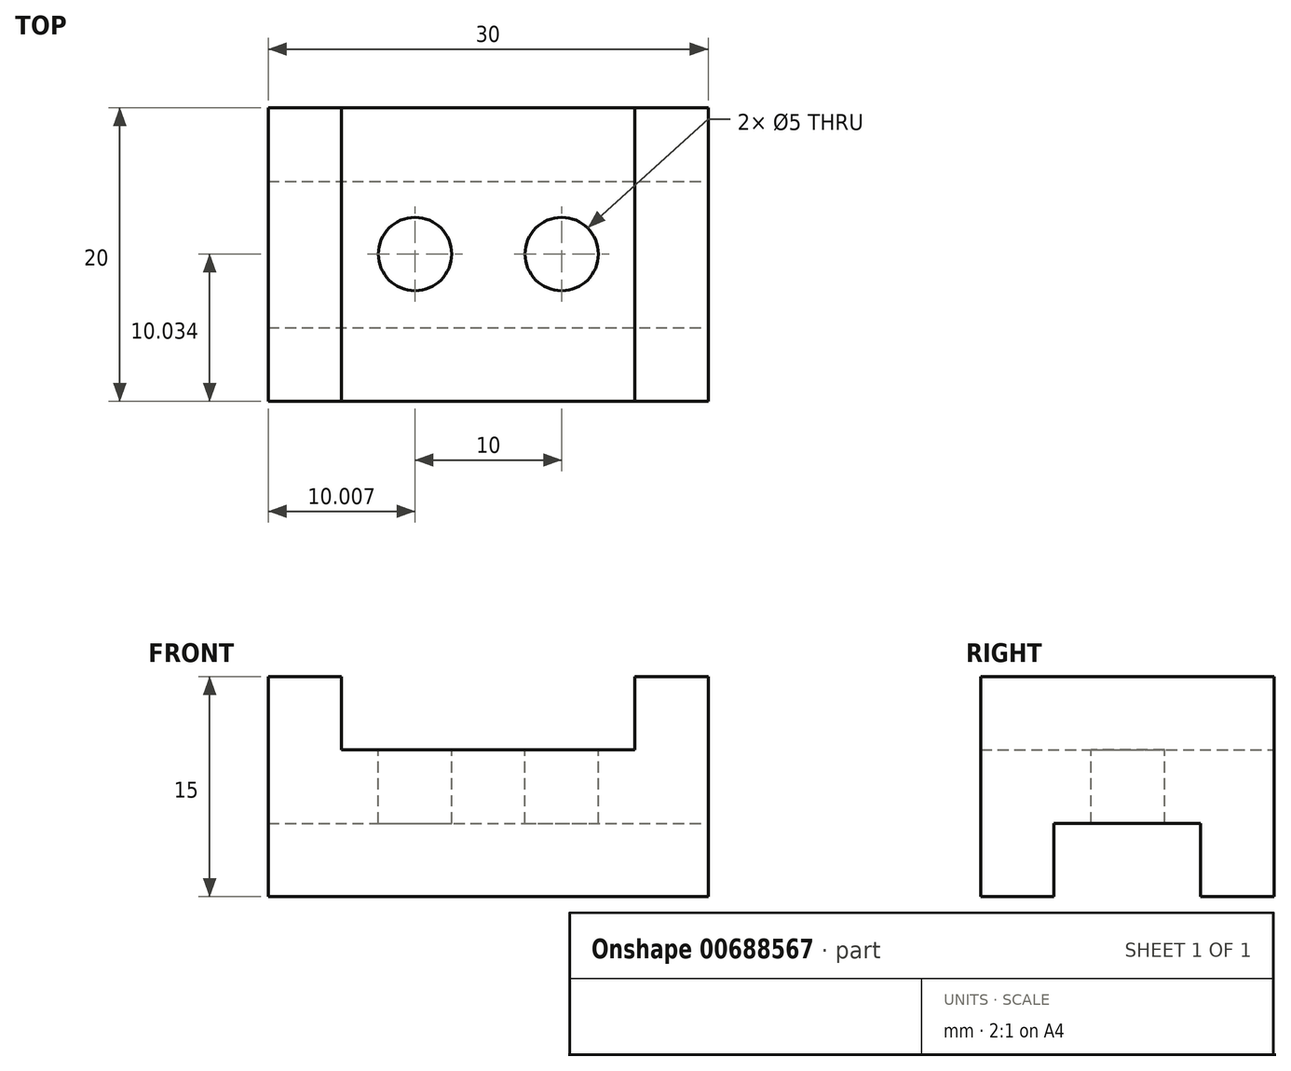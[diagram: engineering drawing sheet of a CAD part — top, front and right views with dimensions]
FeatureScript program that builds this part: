
annotation { "Feature Type Name" : "Feature", "Feature Type Description" : "" }
export const myFeature = defineFeature(function(context is Context, id is Id, definition is map)
    precondition{}
    {
        {
            var Q0;
            Q0=qCreatedBy(makeId("Top.planeOp"),FACE);
            var sketch = newSketch(context, id + "F0", { "sketchPlane" : qUnion([Q0])});
            skLineSegment(sketch, "E0.bottom", {"start": v(19.3, -0.64) * mm, "end": v(-10.7, -0.64) * mm});
            skLineSegment(sketch, "E0.top", {"start": v(19.3, 19.36) * mm, "end": v(-10.7, 19.36) * mm});
            skLineSegment(sketch, "E0.left", {"start": v(19.3, -0.64) * mm, "end": v(19.3, 19.36) * mm});
            skLineSegment(sketch, "E0.right", {"start": v(-10.7, -0.64) * mm, "end": v(-10.7, 19.36) * mm});
            skSolve(sketch);
        }
        {
            var Q0;
            Q0=qSketchRegion(id+"F0",true);
            extrude(context, id + "F1", {"entities" : qUnion([Q0]), "depth" : 15 * mm});
        }
        {
            var Q0;
            Q0=makeQuery(id+"F1.opExtrude","SWEPT_FACE",FACE,{"disambiguationData":[OSD([sQuery(id+"F0.wireOp",EDGE,"E0.left")])]});
            var sketch = newSketch(context, id + "F2", { "sketchPlane" : qUnion([Q0])});
            skLineSegment(sketch, "E1", {"start": v(-0.64, 0) * mm, "end": v(4.36, 0) * mm});
            skLineSegment(sketch, "E2", {"start": v(4.36, 0) * mm, "end": v(4.36, 5) * mm});
            skLineSegment(sketch, "E3", {"start": v(4.36, 5) * mm, "end": v(14.36, 5) * mm});
            skLineSegment(sketch, "E4", {"start": v(14.36, 5) * mm, "end": v(14.36, 0) * mm});
            skLineSegment(sketch, "E5", {"start": v(14.36, 0) * mm, "end": v(19.36, 0) * mm});
            skSolve(sketch);
        }
        {
            var Q0;
            Q0 = qSketchRegion(id + "F2", true);
            var Q1;
            {var subQ0=sQuery(id+"F2.wireOp",EDGE,"E2");Q1=makeQuery(id+"F2.imprint","IMPRINT",FACE,{"disambiguationData":[TD([[makeQuery(id+"F2.imprint","IMPRINT",EDGE,{"derivedFrom":subQ0}),-1.0]])]});}
            extrude(context, id + "F3", {"entities" : qUnion([Q0, Q1]), "operationType" : NewBodyOperationType.REMOVE, "endBound" : BoundingType.THROUGH_ALL, "oppositeDirection" : true, "depth" : 25 * mm, "offsetDistance" : 25 * mm});
        }
        {
            var Q0;
            Q0=makeQuery(id+"F1.opExtrude","SWEPT_FACE",FACE,{"disambiguationData":[OSD([sQuery(id+"F0.wireOp",EDGE,"E0.top")])]});
            var sketch = newSketch(context, id + "F4", { "sketchPlane" : qUnion([Q0])});
            skLineSegment(sketch, "E6", {"start": v(-19.3, 15) * mm, "end": v(-14.3, 15) * mm});
            skLineSegment(sketch, "E7", {"start": v(-14.3, 15) * mm, "end": v(-14.3, 10) * mm});
            skLineSegment(sketch, "E8", {"start": v(-14.3, 10) * mm, "end": v(5.7, 10) * mm});
            skLineSegment(sketch, "E9", {"start": v(5.7, 10) * mm, "end": v(5.7, 15) * mm});
            skLineSegment(sketch, "E10", {"start": v(5.7, 15) * mm, "end": v(10.7, 15) * mm});
            skSolve(sketch);
        }
        {
            var Q0;
            {var subQ0=sQuery(id+"F4.wireOp",EDGE,"E7");Q0=makeQuery(id+"F4.imprint","IMPRINT",FACE,{"disambiguationData":[TD([[makeQuery(id+"F4.imprint","IMPRINT",EDGE,{"derivedFrom":subQ0}),1.0]])]});}
            extrude(context, id + "F5", {"entities" : qUnion([Q0]), "operationType" : NewBodyOperationType.REMOVE, "endBound" : BoundingType.THROUGH_ALL, "oppositeDirection" : true, "depth" : 25 * mm, "offsetDistance" : 25 * mm});
        }
        {
            var Q0;
            Q0=makeQuery(id+"F5.boolean.opBoolean","COPY",FACE,{"derivedFrom":makeQuery(id+"F5.opExtrude","SWEPT_FACE",FACE,{"disambiguationData":[OSD([sQuery(id+"F4.wireOp",EDGE,"E8")])]})});
            var sketch = newSketch(context, id + "F6", { "sketchPlane" : qUnion([Q0])});
            skLineSegment(sketch, "E11", {"start": v(-10.72, -0.64) * mm, "end": v(-10.72, 19.36) * mm});
            skLineSegment(sketch, "E12", {"start": v(-10.72, 19.36) * mm, "end": v(-10.72, 9.36) * mm});
            skLineSegment(sketch, "E13", {"start": v(-10.72, 9.36) * mm, "end": v(19.32, 9.36) * mm});
            skSolve(sketch);
        }
        {
            var Q0;
            {var subQ1=sQuery(id+"F4.wireOp",EDGE,"E8");var subQ6=makeQuery(id+"F5.boolean.opBoolean","INTERSECT",EDGE,{"derivedFrom":[makeQuery(id+"F1.opExtrude","SWEPT_FACE",FACE,{"disambiguationData":[OSD([sQuery(id+"F0.wireOp",EDGE,"E0.bottom")])]}),makeQuery(id+"F5.opExtrude","SWEPT_FACE",FACE,{"disambiguationData":[OSD([subQ1])]})]});Q0=makeQuery(id+"F6.imprint","IMPRINT",FACE,{"disambiguationData":[TD([[makeQuery(id+"F6.imprint","IMPRINT",EDGE,{"derivedFrom":subQ6}),1.0]])]});}
            var sketch = newSketch(context, id + "F7", { "sketchPlane" : qUnion([Q0])});
            skCircle(sketch, "E14", {"center": v(-0.68, 9.4) * mm, "radius": 2.5 * mm});
            skCircle(sketch, "E15", {"center": v(9.32, 9.4) * mm, "radius": 2.5 * mm});
            skSolve(sketch);
        }
        {
            var Q0;
            Q0 = qSketchRegion(id + "F7", true);
            extrude(context, id + "F8", {"entities" : qUnion([Q0]), "operationType" : NewBodyOperationType.REMOVE, "endBound" : BoundingType.THROUGH_ALL, "oppositeDirection" : true, "depth" : 25 * mm, "offsetDistance" : 25 * mm});
        }
    });
